# Revit family: VIESSMANN - Energycal AWH Pro AT 200-235
name_source: partatom
category: Wyposażenie mechaniczne
revit_build: Autodesk Revit 2017 (Build: 20160720_1515(x64)
units: mm (PartAtom-declared; Revit-internal decimal feet)

## family parameters
Numer OmniClass = 23.75.10.21.11
Oparty na płaszczyźnie roboczej = Nie
Punkt obliczania pomieszczeń = Nie
Tnij formami wycięć po wczytaniu = Nie
Typ części = Normalny
Tytuł OmniClass = Air-Source Heat Pumps
Współdzielony = Nie
Wymiar okrągłego złącza = Użyj średnicy
Zawsze pionowo = Tak

## types (2) — shared parameters
Autor = www.archispace.pl
Całkowite napełnienie czynnikiem chłodniczym = 73.00 kg
Częstotliwość = 50 Hz
Głębokość = 1208 mm  [stored 3.96325 ft]
Ilość/Obiegi chłodnicze sprężarki (nr/nr) = 2/2
Klasa energetyczna = A+
Liczba biegunów = 3
Liczba wentylatorów = 4
Moc nominalna silnika pompy obiegowej = 3 kW
Moc nominalna wentylatora = 2 kW
Model = Powietrzna pompa ciepła Energycal AWH PRO AT / Air-water heat pump Energycal AWH PRO AT
Naczynie wzbiorcze = 18 m³
Napięcie zasilania = 400 V
Nominalna moc pompy = 3 kW
Opis = Energycal AWH Pro AT to typoszereg wysokotemperaturowych pomp ciepła z czynnikiem chłodniczym R134a lub R513A osiągających na zasilaniu temperatury wody do 80°C.
Pojemność zbiornika buforowego = 450 m³
Poziom ciśnienia akustycznego dB(A) = 65 mm  [stored 0.213255 ft]
Poziom mocy akustycznej - wersja cicha LN dB(A) = 95 mm
Poziom mocy akustycznej dB(A) = 97 mm  [stored 0.318241 ft]
Połączenia hydrauliczne = 3"
Producent = Viessmann Sp. z o.o
Przód = 3677 mm  [stored 12.0636 ft]
Prąd nominalny silnika pompy obiegowej = 6 A
Prąd nominalny wentylatora = 4 A
Stopień wydajności = 4
Strefa serwisowa_przód = 1000 mm  [stored 3.28084 ft]
Strefa serwisowa_szerokość = 1500 mm  [stored 4.92126 ft]
Strefa serwisowa_tył = 2000 mm  [stored 6.56168 ft]
Strefa serwisowa_wysokość = 1958 mm
Szerokość = 5390 mm  [stored 17.6837 ft]
Typ sprężarki = Reciprocating
Typ wentylatora = Osiowy
Typ wymiennika po stronie grzewczej = Plate exchanger
Tył = 1657 mm
URL = https://www.viessmann-projektant.pl
Viessmann Kolor 1 = Viessmann Kolor 2
Współczynnik mocy = 1
Wysokość = 2390 mm  [stored 7.84121 ft]
Zasilanie elektryczne (V/ph/Hz) = 400/3N~/50+5%
Zasilanie pomocnicze (V/ph/Hz) = 230/1N~/50+5%
zero-valued in all types: Poziom ciśnienia akustycznego - wersja super cicha SLN dB(A), Poziom mocy akustycznej - wersja super cicha SLN dB(A)

## per-type parameters (varying)
| type | Całkowite napełnienie olejem | Ciśnienie podnoszenia pompy (A7W45) | Efektywność sezonowa ηs | Maksymalna moc pobierania | Maksymalny pobór prądu | Maksymalny prąd rozruchowy | Natężenie przepływu wody (A7W45) | Natężenie przepływu wody (A7W45) l/h | Nominalna moc grzewcza (A7W45) | Obciążenie pozorne | Pobór mocy elektrycznej (A7W45) | Poziom ciśnienia akustycznego - wersja cicha LN dB(A) | Przepływ powietrza | SCOP | Spadek ciśnienia wody (A7W45) | Współczynnik efektywności [COP] (A7W45) |
| Wielkość jednostki - 200 | 14.80 kg | 173.0 kPa | 110.9 % | 121 kW | 258 A | 491 A | 9.9 L/s | 35593 | 206 kW | 121400 VA | 63 kW | 59 mm | 92400.0 m³/h | 2.85 | 25.0 kPa | 3.28 |
| Wielkość jednostki - 235 | 10.00 kg | 145.0 kPa | 113.6 % | 132 kW | 314 A | 545 A | 10.8 L/s | 38704 | 224 kW | 132000 VA | 67 kW | 63 mm  [stored 0.206693 ft] | 91200.0 m³/h | 2.92 | 24.0 kPa | 3.35 |

note: [stored X ft] marks values corroborated as IEEE doubles in the binary element streams (Revit-internal decimal feet)
